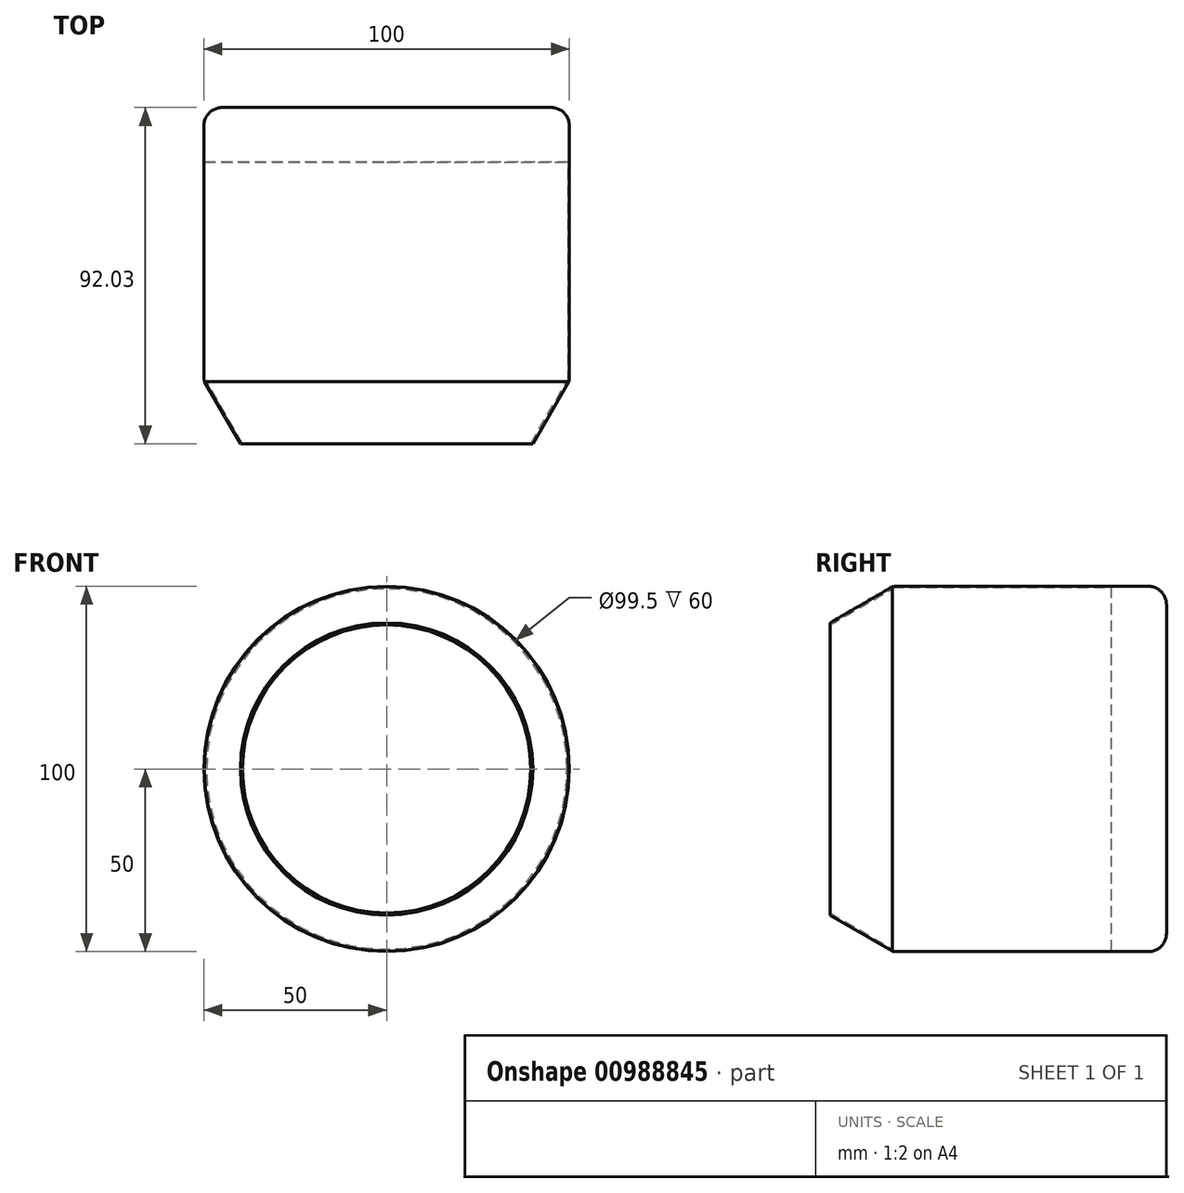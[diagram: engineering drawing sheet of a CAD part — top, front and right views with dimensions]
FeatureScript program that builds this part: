
annotation { "Feature Type Name" : "Feature", "Feature Type Description" : "" }
export const myFeature = defineFeature(function(context is Context, id is Id, definition is map)
    precondition{}
    {
        {
            var Q0;
            Q0=qCreatedBy(makeId("Front.planeOp"),FACE);
            var sketch = newSketch(context, id + "F0", { "sketchPlane" : qUnion([Q0])});
            skCircle(sketch, "E0", {"center": v(0, 0) * mm, "radius": 50 * mm});
            skSolve(sketch);
        }
        {
            var Q0;
            Q0 = qSketchRegion(id + "F0", true);
            extrude(context, id + "F1", {"entities" : qUnion([Q0]), "depth" : 15 * mm, "offsetDistance" : 25 * mm});
        }
        {
            var Q0;
            Q0=makeQuery(id+"F1.opExtrude","CAP_FACE",FACE,{"disambiguationData":[OSD([sQuery(id+"F0.wireOp",EDGE,"E0")])],"isStart":false});
            var sketch = newSketch(context, id + "F2", { "sketchPlane" : qUnion([Q0])});
            skCircle(sketch, "E1", {"center": v(0, 0) * mm, "radius": 50 * mm});
            skCircle(sketch, "E2", {"center": v(0, 0) * mm, "radius": 49.75 * mm});
            skSolve(sketch);
        }
        {
            var Q0;
            Q0 = qSketchRegion(id + "F2", true);
            extrude(context, id + "F3", {"entities" : qUnion([Q0]), "operationType" : NewBodyOperationType.ADD, "depth" : 60 * mm, "offsetDistance" : 25 * mm});
        }
        {
            var Q0;
            Q0=qCreatedBy(makeId("Top.planeOp"),FACE);
            var sketch = newSketch(context, id + "F4", { "sketchPlane" : qUnion([Q0])});
            skLineSegment(sketch, "E3", {"start": v(0, -72.03) * mm, "end": v(0, -92.03) * mm});
            skLineSegment(sketch, "E4", {"start": v(-39.42, -92.03) * mm, "end": v(-40, -92.03) * mm});
            skLineSegment(sketch, "E5", {"start": v(0, -75) * mm, "end": v(-49.87, -75) * mm});
            skLineSegment(sketch, "E6", {"start": v(-49.87, -75) * mm, "end": v(-40, -92.03) * mm});
            skLineSegment(sketch, "E7.0", {"start": v(50, -75) * mm, "end": v(-50, -75) * mm});
            skLineSegment(sketch, "E8.0", {"start": v(-49.29, -75) * mm, "end": v(-39.42, -92.03) * mm});
            skSolve(sketch);
        }
        {
            var Q0;
            {var subQ0=sQuery(id+"F4.wireOp",EDGE,"E4");Q0=makeQuery(id+"F4.imprint","IMPRINT",FACE,{"disambiguationData":[TD([[makeQuery(id+"F4.imprint","IMPRINT",EDGE,{"derivedFrom":subQ0}),-1.0]])]});}
            var Q1;
            Q1=sQuery(id+"F4.wireOp",EDGE,"E3");
            revolve(context, id + "F5", {"operationType" : NewBodyOperationType.ADD, "surfaceOperationType" : NewSurfaceOperationType.NEW, "entities" : qUnion([Q0]), "axis" : qUnion([Q1]), "revolveType" : RevolveType.FULL});
        }
        {
            var Q0;
            Q0=makeQuery(id+"F1.opExtrude","CAP_EDGE",EDGE,{"disambiguationData":[OSD([sQuery(id+"F0.wireOp",EDGE,"E0")])],"isStart":true});
            fillet(context, id + "F6", {"entities" : qUnion([Q0]), "radius" : 5 * mm, "tangentPropagation" : true, "allowEdgeOverflow" : false});
        }
        {
            var Q0;
            Q0=makeQuery(id+"F3.opExtrude","CAP_EDGE",EDGE,{"disambiguationData":[OSD([sQuery(id+"F2.wireOp",EDGE,"E1")])],"isStart":false});
            fillet(context, id + "F7", {"entities" : qUnion([Q0]), "radius" : 10 * mm, "tangentPropagation" : true, "allowEdgeOverflow" : false});
        }
    });
